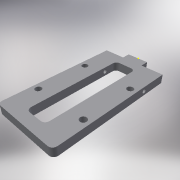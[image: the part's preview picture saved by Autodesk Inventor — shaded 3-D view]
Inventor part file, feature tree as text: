
AUTODESK INVENTOR PART (.ipt)
format: ipt  version: 2016 (Build 200138000, 138)  size: 172,032 bytes
history: native  units: mm
features: sketch x5, extrude x4, projected_geometry x3, fillet x1
ambient origin geometry x8: Origin, YZ Plane, XZ Plane, XY Plane, X Axis, Y Axis, Z Axis, Center Point
bodies: Solid1 (feature_tree)
feature tree (13):
  extrude  "Extrusion1"  Depth=60.0mm
  extrude  "Extrusion2"  Depth=15.0mm
  sketch  "Sketch3"  dims[d6=12.0mm d7=3.0mm]
  fillet  "Fillet1"  Radius=3.0mm
  extrude  "Extrusion3"  Depth=3.0mm
  extrude  "Extrusion4"  Depth=24.0mm
  sketch  "Sketch1"  dims[d0=30.0mm d1=60.0mm]
  sketch  "Sketch2"  dims[d2=4.0mm d3=0.0mm d4=15.0mm d5=3.0mm]
  projected_geometry  "Projected Loop1"
  sketch  "Sketch4"  dims[d8=12.0mm d9=24.0mm]
  projected_geometry  "Projected Loop2"
  sketch  "Sketch5"  dims[d10=15.0mm d11=4.0mm d12=0.0mm d13=4.0mm d14=10.0mm d15=5.0mm d16=10.0mm d18=5.0mm d19=2.0mm d20=2.0mm d21=2.0mm d22=4.0mm d23=0.0mm d24=2.0mm d25=14.0mm d26=4.0mm d27=0.0mm d28=10.0mm]
  projected_geometry  "Projected Loop3"
